# Revit family: 48653USA_new
name_source: partatom
category: Plumbing Fixtures
revit_build: Autodesk Revit 2018 (Build: 20170223_1515(x64)
units: mm (PartAtom-declared; Revit-internal decimal feet)

## family parameters
Always vertical = No
Cut with Voids When Loaded = No
OmniClass Number = 23.40.20.00
OmniClass Title = General Furniture and Specialties
Part Type = Normal
Room Calculation Point = No
Round Connector Dimension = Use Diameter
Shared = No
Work Plane-Based = No

## types (2) — shared parameters
Always visible = Yes
BIMobject category = Other Sanitary
Design country = Germany
EAN code = 4059625330395
Edition number = 1
IFC Classification = Sanitary Terminal
Installation instructions = https://www.axor-design.com
Manufacturer country = Germany
Manufacturer name = AXOR
Material 2 = AXOR - AXOR One - Graphite
Material 3 = AXOR - AXOR One - 001 Chrome
Material main = Chrome
Product Guid = e1970c4d-4293-40dc-a47d-f663cf06a3f6
Product SKU = 48653USA
Product data url = https://www.bimobject.com
Product family = AXOR One
Product group = Hand showers
Product name = 48653USA AXOR One Hand shower 75 1jet 2.5 GPM
Product url = https://www.axor-design.com
QR code = https://www.bimobject.com
Technical description = https://www.axor-design.com

## per-type parameters (varying)
| type | Material 1 |
| 671 Matte Black | AXOR - AXOR One - 671 Matte Black |
| 001 Chrome | AXOR - AXOR One - 001 Chrome |

## geometry (parser evidence)
native form markers: Sweep x3
no freeform markers — native parametric forms only
